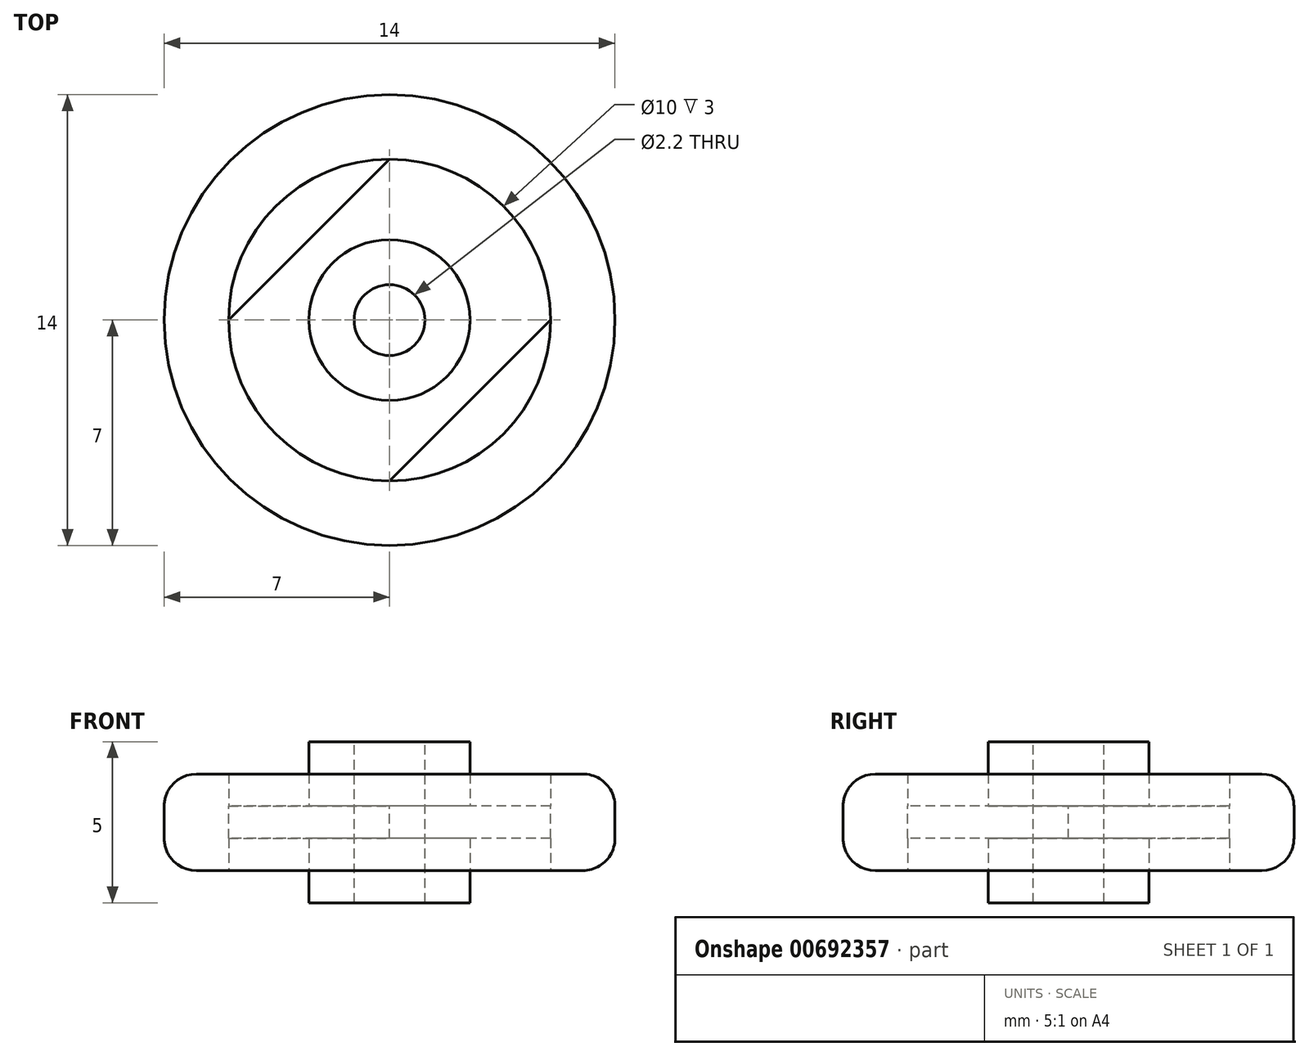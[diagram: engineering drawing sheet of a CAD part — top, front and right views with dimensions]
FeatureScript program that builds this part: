
annotation { "Feature Type Name" : "Feature", "Feature Type Description" : "" }
export const myFeature = defineFeature(function(context is Context, id is Id, definition is map)
    precondition{}
    {
        {
            var Q0;
            Q0=qCreatedBy(makeId("Top.planeOp"),FACE);
            var sketch = newSketch(context, id + "F0", { "sketchPlane" : qUnion([Q0])});
            skCircle(sketch, "E0", {"center": v(0, 0) * mm, "radius": 7 * mm});
            skCircle(sketch, "E1", {"center": v(0, 0) * mm, "radius": 5 * mm});
            skCircle(sketch, "E2", {"center": v(0, 0) * mm, "radius": 2.5 * mm});
            skSolve(sketch);
        }
        {
            var Q0;
            Q0=makeQuery(id+"F0.imprint","IMPRINT",FACE,{"disambiguationData":[TD([[makeQuery(id+"F0.imprint","IMPRINT",EDGE,{"derivedFrom":sQuery(id+"F0.wireOp",EDGE,"E0")}),1.0]])]});
            extrude(context, id + "F1", {"entities" : qUnion([Q0]), "depth" : 3 * mm, "offsetDistance" : 25 * mm});
        }
        {
            var Q0;
            Q0=makeQuery(id+"F0.imprint","IMPRINT",FACE,{"disambiguationData":[TD([[makeQuery(id+"F0.imprint","IMPRINT",EDGE,{"derivedFrom":sQuery(id+"F0.wireOp",EDGE,"E1")}),1.0]])]});
            extrude(context, id + "F2", {"entities" : qUnion([Q0]), "operationType" : NewBodyOperationType.ADD, "depth" : 2 * mm, "offsetDistance" : 25 * mm, "hasSecondDirection" : true, "secondDirectionOppositeDirection" : true, "secondDirectionDepth" : -1 * mm});
        }
        {
            var Q0;
            Q0=makeQuery(id+"F0.imprint","IMPRINT",FACE,{"disambiguationData":[TD([[makeQuery(id+"F0.imprint","IMPRINT",EDGE,{"derivedFrom":sQuery(id+"F0.wireOp",EDGE,"E2")}),1.0]])]});
            extrude(context, id + "F3", {"entities" : qUnion([Q0]), "operationType" : NewBodyOperationType.ADD, "depth" : 4 * mm, "offsetDistance" : 25 * mm, "hasSecondDirection" : true, "secondDirectionOppositeDirection" : true, "secondDirectionDepth" : 1 * mm});
        }
        {
            var Q0;
            Q0=makeQuery(id+"F3.opExtrude","CAP_FACE",FACE,{"disambiguationData":[OSD([sQuery(id+"F0.wireOp",EDGE,"E2")])],"isStart":false});
            var sketch = newSketch(context, id + "F4", { "sketchPlane" : qUnion([Q0])});
            skPoint(sketch, "E3", {"position": v(0, 0) * mm});
            skSolve(sketch);
        }
        {
            var Q0;
            Q0=sQuery(id+"F4.wireOp",VERTEX,"E3");
            var Q1;
            Q1=makeQuery(id+"F1.opExtrude","SWEPT_BODY",BODY,{"disambiguationData":[OSD([sQuery(id+"F0.wireOp",EDGE,"E0"),sQuery(id+"F0.wireOp",EDGE,"E1")])]});
            hole(context, id + "F5", {"style" : HoleStyle.SIMPLE, "endStyle" : HoleEndStyle.THROUGH, "holeDiameter" : 2.2 * mm, "majorDiameter" : 5 * mm, "isTappedThrough" : true, "tappedDepth" : 12 * mm, "tapClearance" : 3, "locations" : qUnion([Q0]), "scope" : qUnion([Q1])});
        }
        {
            var Q0;
            Q0=makeQuery(id+"F1.opExtrude","CAP_EDGE",EDGE,{"disambiguationData":[OSD([sQuery(id+"F0.wireOp",EDGE,"E0")])],"isStart":false});
            var Q1;
            Q1=makeQuery(id+"F1.opExtrude","CAP_EDGE",EDGE,{"disambiguationData":[OSD([sQuery(id+"F0.wireOp",EDGE,"E0")])],"isStart":true});
            fillet(context, id + "F6", {"entities" : qUnion([Q0, Q1]), "radius" : 1 * mm, "tangentPropagation" : true, "allowEdgeOverflow" : false});
        }
        {
            var Q0;
            Q0=makeQuery(id+"F2.opExtrude","CAP_FACE",FACE,{"disambiguationData":[OSD([sQuery(id+"F0.wireOp",EDGE,"E1"),sQuery(id+"F0.wireOp",EDGE,"E2")])],"isStart":false});
            var sketch = newSketch(context, id + "F7", { "sketchPlane" : qUnion([Q0])});
            skLineSegment(sketch, "E4", {"start": v(0, 0) * mm, "end": v(5, 0) * mm});
            skLineSegment(sketch, "E5", {"start": v(5, 0) * mm, "end": v(0, -5) * mm});
            skLineSegment(sketch, "E6", {"start": v(0, -5) * mm, "end": v(0, 5) * mm});
            skLineSegment(sketch, "E7", {"start": v(0, 5) * mm, "end": v(-5, 0) * mm});
            skSolve(sketch);
        }
        {
            var Q0;
            {var subQ0=sQuery(id+"F7.wireOp",EDGE,"E7");Q0=makeQuery(id+"F7.imprint","IMPRINT",FACE,{"disambiguationData":[TD([[makeQuery(id+"F7.imprint","IMPRINT",EDGE,{"derivedFrom":subQ0}),-1.0]])]});}
            var Q1;
            {var subQ0=sQuery(id+"F7.wireOp",EDGE,"E5");Q1=makeQuery(id+"F7.imprint","IMPRINT",FACE,{"disambiguationData":[TD([[makeQuery(id+"F7.imprint","IMPRINT",EDGE,{"derivedFrom":subQ0}),1.0]])]});}
            extrude(context, id + "F8", {"entities" : qUnion([Q0, Q1]), "operationType" : NewBodyOperationType.REMOVE, "oppositeDirection" : true, "depth" : 3 * mm, "offsetDistance" : 25 * mm});
        }
    });
